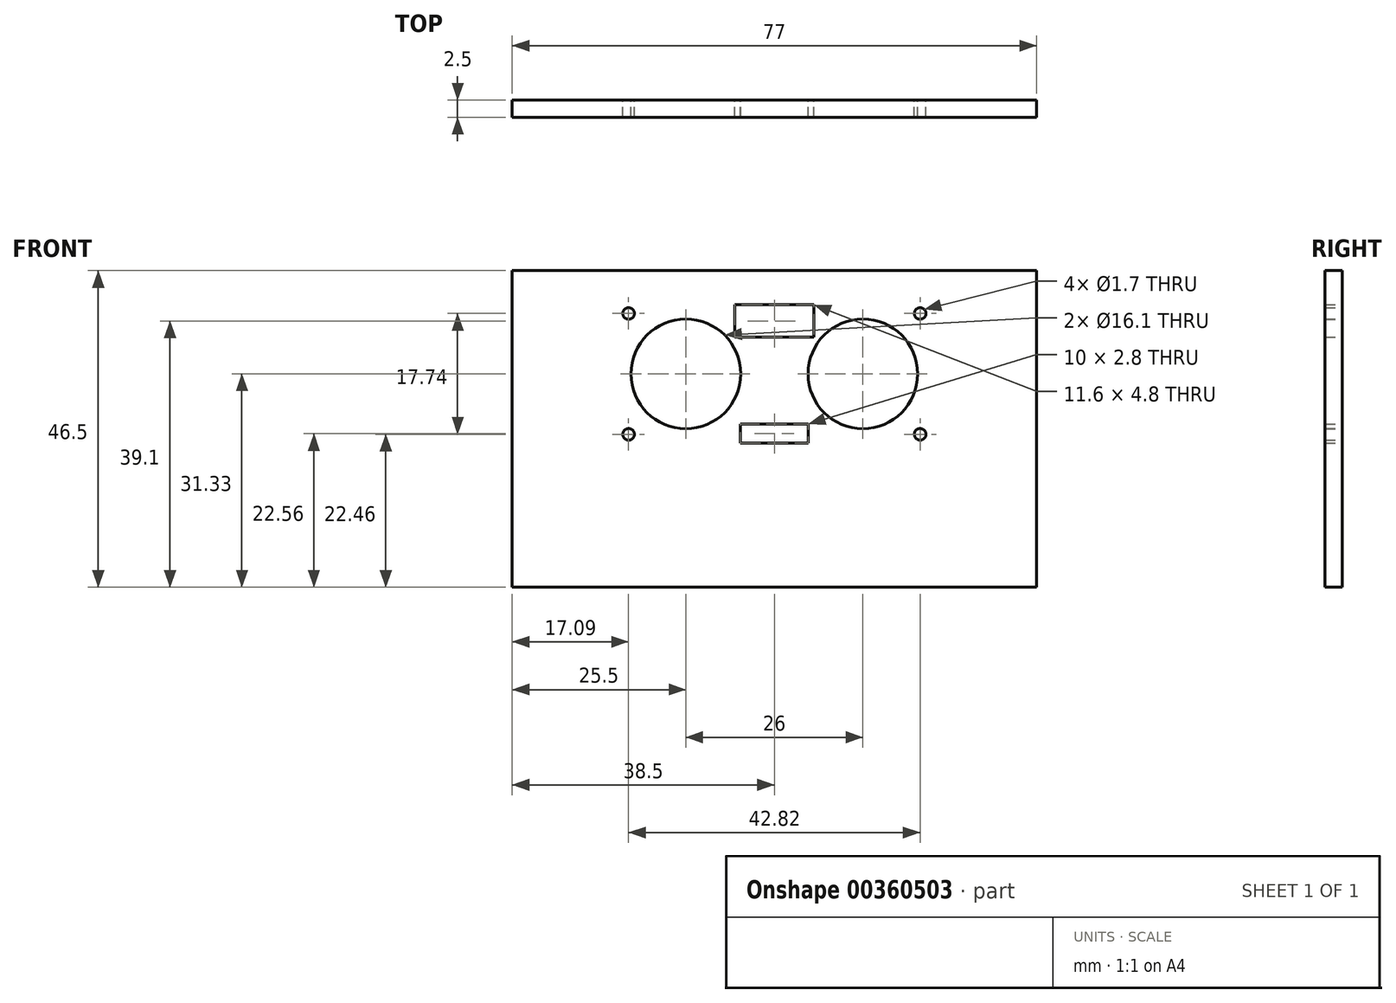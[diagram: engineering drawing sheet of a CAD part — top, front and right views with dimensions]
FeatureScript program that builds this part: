
annotation { "Feature Type Name" : "Feature", "Feature Type Description" : "" }
export const myFeature = defineFeature(function(context is Context, id is Id, definition is map)
    precondition{}
    {
        {
            var Q0;
            Q0=qCreatedBy(makeId("Front.planeOp"),FACE);
            var sketch = newSketch(context, id + "F0", { "sketchPlane" : qUnion([Q0])});
            skLineSegment(sketch, "E0.bottom", {"start": v(0, 0) * mm, "end": v(83, 0) * mm, "construction": true});
            skLineSegment(sketch, "E0.top", {"start": v(0, 52.5) * mm, "end": v(83, 52.5) * mm, "construction": true});
            skLineSegment(sketch, "E0.left", {"start": v(0, 0) * mm, "end": v(0, 52.5) * mm, "construction": true});
            skLineSegment(sketch, "E0.right", {"start": v(83, 0) * mm, "end": v(83, 52.5) * mm, "construction": true});
            skLineSegment(sketch, "E1.0", {"start": v(3, 3) * mm, "end": v(3, 49.5) * mm});
            skLineSegment(sketch, "E1.1", {"start": v(3, 3) * mm, "end": v(80, 3) * mm});
            skLineSegment(sketch, "E1.2", {"start": v(80, 3) * mm, "end": v(80, 49.5) * mm});
            skLineSegment(sketch, "E1.3", {"start": v(3, 49.5) * mm, "end": v(80, 49.5) * mm});
            skLineSegment(sketch, "E2.bottom", {"start": v(64.2, 44.5) * mm, "end": v(18.8, 44.5) * mm, "construction": true});
            skLineSegment(sketch, "E2.top", {"start": v(64.2, 24.16) * mm, "end": v(18.8, 24.16) * mm, "construction": true});
            skLineSegment(sketch, "E2.left", {"start": v(64.21, 44.5) * mm, "end": v(64.21, 24.16) * mm, "construction": true});
            skLineSegment(sketch, "E2.right", {"start": v(18.79, 44.5) * mm, "end": v(18.8, 24.16) * mm, "construction": true});
            skLineSegment(sketch, "E3", {"start": v(41.5, 44.5) * mm, "end": v(41.5, 24.16) * mm, "construction": true});
            skLineSegment(sketch, "E4", {"start": v(18.8, 34.33) * mm, "end": v(64.21, 34.33) * mm, "construction": true});
            skCircle(sketch, "E5", {"center": v(54.5, 34.33) * mm, "radius": 8.05 * mm});
            skLineSegment(sketch, "E6", {"start": v(35.7, 44.5) * mm, "end": v(41.5, 44.5) * mm});
            skLineSegment(sketch, "E7", {"start": v(35.7, 44.5) * mm, "end": v(35.7, 39.7) * mm});
            skLineSegment(sketch, "E8", {"start": v(41.5, 39.7) * mm, "end": v(35.7, 39.7) * mm});
            skLineSegment(sketch, "E9", {"start": v(36.5, 26.96) * mm, "end": v(41.5, 26.96) * mm});
            skLineSegment(sketch, "E10", {"start": v(36.5, 26.96) * mm, "end": v(36.5, 24.16) * mm});
            skLineSegment(sketch, "E11", {"start": v(41.5, 24.16) * mm, "end": v(36.5, 24.16) * mm});
            skLineSegment(sketch, "E12.MirrorCS", {"start": v(41.5, 39.7) * mm, "end": v(47.3, 39.7) * mm});
            skLineSegment(sketch, "E13.MirrorCS", {"start": v(47.3, 44.5) * mm, "end": v(47.3, 39.7) * mm});
            skCircle(sketch, "E14.MirrorC", {"center": v(28.5, 34.33) * mm, "radius": 8.05 * mm});
            skLineSegment(sketch, "E15.MirrorCS", {"start": v(46.5, 26.96) * mm, "end": v(41.5, 26.96) * mm});
            skLineSegment(sketch, "E16.MirrorCS", {"start": v(46.5, 26.96) * mm, "end": v(46.5, 24.16) * mm});
            skLineSegment(sketch, "E17.MirrorCS", {"start": v(18.8, 24.16) * mm, "end": v(64.2, 24.16) * mm, "construction": true});
            skLineSegment(sketch, "E18", {"start": v(47.3, 44.5) * mm, "end": v(41.5, 44.5) * mm});
            skLineSegment(sketch, "E19", {"start": v(46.5, 24.16) * mm, "end": v(41.5, 24.16) * mm});
            skCircle(sketch, "E20", {"center": v(62.91, 43.2) * mm, "radius": 0.85 * mm});
            skCircle(sketch, "E21.MirrorC", {"center": v(62.91, 25.46) * mm, "radius": 0.85 * mm});
            skCircle(sketch, "E22.MirrorC", {"center": v(20.09, 43.2) * mm, "radius": 0.85 * mm});
            skCircle(sketch, "E23.MirrorC", {"center": v(20.09, 25.46) * mm, "radius": 0.85 * mm});
            skLineSegment(sketch, "E24", {"start": v(41.5, 44.5) * mm, "end": v(41.5, 49.5) * mm, "construction": true});
            skSolve(sketch);
        }
        {
            var Q0;
            Q0=qSketchRegion(id+"F0",true);
            extrude(context, id + "F1", {"entities" : qUnion([Q0]), "depth" : 2.5 * mm});
        }
    });
